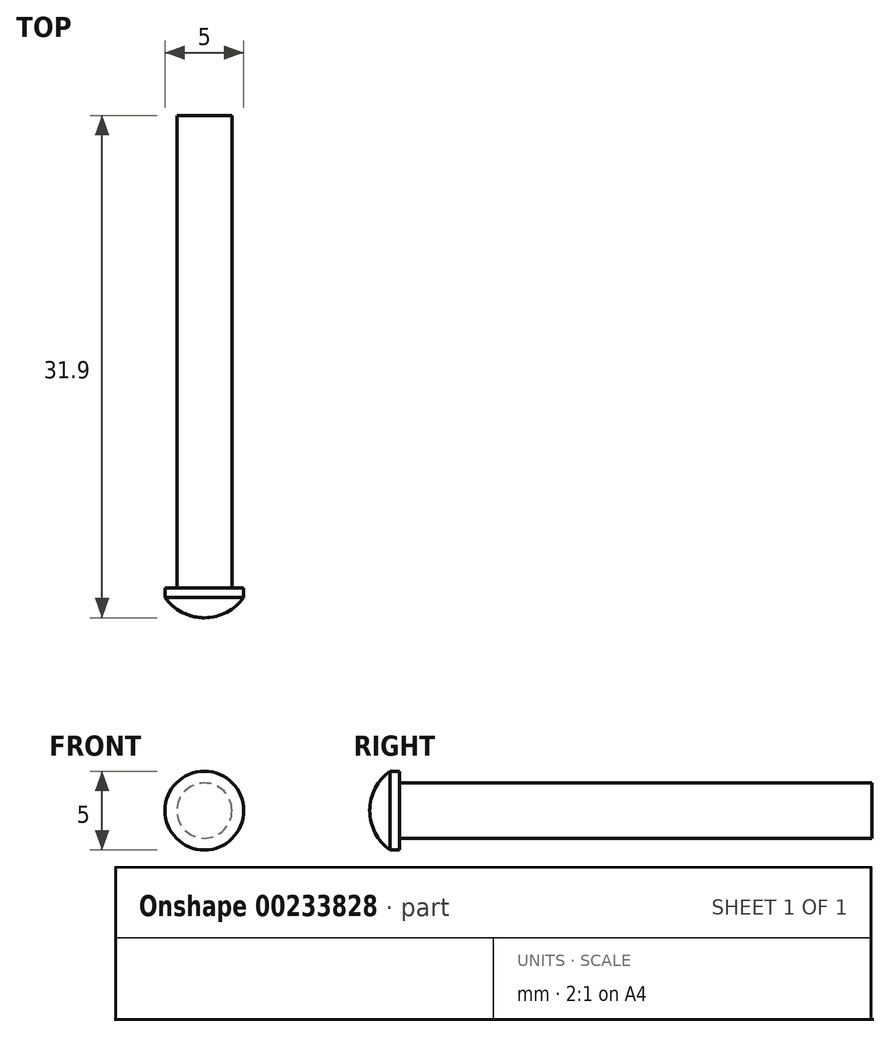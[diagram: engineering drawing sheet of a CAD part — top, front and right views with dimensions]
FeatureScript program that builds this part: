
annotation { "Feature Type Name" : "Feature", "Feature Type Description" : "" }
export const myFeature = defineFeature(function(context is Context, id is Id, definition is map)
    precondition{}
    {
        {
            var Q0;
            Q0=qCreatedBy(makeId("Front.planeOp"),FACE);
            var sketch = newSketch(context, id + "F0", { "sketchPlane" : qUnion([Q0])});
            skCircle(sketch, "E0", {"center": v(0, 0) * mm, "radius": 1.75 * mm});
            skSolve(sketch);
        }
        {
            var Q0;
            Q0=makeQuery(id+"F0.imprint","IMPRINT",FACE,{"disambiguationData":[TD([[makeQuery(id+"F0.imprint","IMPRINT",EDGE,{"derivedFrom":sQuery(id+"F0.wireOp",EDGE,"E0")}),1.0]])]});
            extrude(context, id + "F1", {"entities" : qUnion([Q0]), "endBound" : BoundingType.SYMMETRIC, "depth" : 30 * mm});
        }
        {
            var Q0;
            Q0=makeQuery(id+"F1.opExtrude","CAP_FACE",FACE,{"disambiguationData":[OSD([sQuery(id+"F0.wireOp",EDGE,"E0")])],"isStart":false});
            var sketch = newSketch(context, id + "F2", { "sketchPlane" : qUnion([Q0])});
            skCircle(sketch, "E1", {"center": v(0, 0) * mm, "radius": 2.5 * mm});
            skSolve(sketch);
        }
        {
            var Q0;
            Q0=makeQuery(id+"F2.imprint","IMPRINT",FACE,{"disambiguationData":[TD([[makeQuery(id+"F2.imprint","IMPRINT",EDGE,{"derivedFrom":sQuery(id+"F2.wireOp",EDGE,"E1")}),1.0]])]});
            var Q1;
            Q1=makeQuery(id+"F2.imprint","IMPRINT",FACE,{"disambiguationData":[TD([[makeQuery(id+"F2.imprint","IMPRINT",EDGE,{"derivedFrom":makeQuery(id+"F1.opExtrude","CAP_EDGE",EDGE,{"disambiguationData":[OSD([sQuery(id+"F0.wireOp",EDGE,"E0")])],"isStart":false})}),1.0]])]});
            extrude(context, id + "F3", {"entities" : qUnion([Q0, Q1]), "operationType" : NewBodyOperationType.ADD, "depth" : .6 * mm});
        }
        {
            var Q0;
            Q0=qCreatedBy(makeId("Top.planeOp"),FACE);
            var sketch = newSketch(context, id + "F4", { "sketchPlane" : qUnion([Q0])});
            skLineSegment(sketch, "E2.0", {"start": v(2.5, -15.6) * mm, "end": v(-2.5, -15.6) * mm});
            skArc(sketch, "E3", {"start": v(-2.5, -15.6) * mm, "mid": v(-1.4, -16.56) * mm, "end": v(0, -16.9) * mm});
            skLineSegment(sketch, "E4", {"start": v(-2.5, -15.6) * mm, "end": v(0, -15.6) * mm});
            skLineSegment(sketch, "E5", {"start": v(0, -13.85) * mm, "end": v(0, -18.52) * mm});
            skPoint(sketch, "E6.orphan", {"position": v(-3.64, -15.6) * mm});
            skSolve(sketch);
        }
        {
            var Q0;
            Q0 = qSketchRegion(id + "F4", true);
            var Q1;
            Q1=sQuery(id+"F4.wireOp",EDGE,"E5");
            revolve(context, id + "F5", {"operationType" : NewBodyOperationType.ADD, "entities" : qUnion([Q0]), "axis" : qUnion([Q1]), "revolveType" : RevolveType.FULL});
        }
    });
